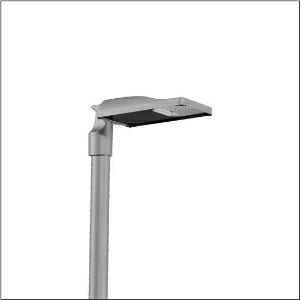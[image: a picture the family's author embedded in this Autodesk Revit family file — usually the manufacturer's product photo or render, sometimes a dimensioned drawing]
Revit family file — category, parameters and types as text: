
# Revit family: streetlight_sl_31_micro___st1_0a_5xh1d71b08ca_ebbd
name_source: partatom
category: Lighting Fixtures
units: mm (PartAtom-declared; Revit-internal decimal feet)

## family parameters
Cut with Voids When Loaded = No
Host = Face
Light Source = No
Part Type = Normal
Room Calculation Point = No
Round Connector Dimension = Use Diameter
Shared = No

## types (1)
- --- (1 x LED, 1170 lm, 10.3 W, 2200K)
    Apparent Load = 10 VA
    CIE Flux Codes = 37 72 97 100 100
    Color Rendering = 70
    Color Temperature = 2200K
    Default Elevation = 1800 mm
    Description = Streetlight SL 31 micro Easy, LST, Desk-Remote mast luminaire for post-top, side-entry; light control with lens of PMMA; light distribution: ST1.0a, direct asymmetric distribution, for standard-compliant lighting for roads and squares; LED: luminous flux: 1.170lm, light colour: 722, colour temperature: 2200K; luminous efficacy: 113,6lm/W; control: pre-setting: linear dimming characteristic, flexible luminous flux parameterisation, time-dependent luminous flux control, constant luminous flux control, power reduction, intelligent temperature release in ECG and LED module, overheat protection; luminaire housing, of diecast aluminium, SITECO metallic grey (DB 702S), corrosivity category C5 high according to DIN EN ISO 12944; cover of toughened safety glass, transparent, mast flange of diecast aluminium, SITECO metallic grey (DB 702S), spigot size: 76/60mm, mast flange included unmounted; cable length: 5,5m, connection cable pre-assembled; mains connection: 220..240V, AC, 50/60Hz; power consumption (at start of service life): 10,3W / (at end of service life): 10,6W / (with reduced operation 50%): 5,3W; protection rating (complete): IP66; insulation class (complete): insulation class II (safety insulation); impact resistance: IK10; certification: CE, ENEC, ENEC+, VDE, UKCA; permissible operating ambient temperature for outdoor applications: -40..+50°C; packaging unit: 1 piece

Light Distribution: ST1.0a
    Height = 76 mm
    Lamp = 1 x LED
    Lamp Light Flux = 1170 lm
    Lamp Power = 10.3 W
    Lamp count = 1
    Length = 467 mm
    Luminous efficacy = 114 lm/W
    Manufacturer = Siteco
    ModVariant = No
    Model = 5XH1D71B08CA
    Number of Poles = 1
    OnlyDefault = Yes
    Power Factor = 1
    Product Name = Streetlight SL 31 micro | ST1.0a
    Product group = mast luminaire | pylon top
    ProductGroupID = 6100
    Protection Class = Protection class II
    Protection Degree = IP 66
    RLX_Detail_Level = 1
    RLX_Emergency_Light_Flux = 0 lm
    RLX_Emergency_Type = 0
    RLX_Emergency_Type_DB = No
    RlxData = <blob elided: 22477 chars, md5=f99bd578>
    Socket = socket
    Standby Power = 0 W
    System Light Flux = 1170 lm
    System Power = 10 W
    Type Comments = factory setting: luminous flux: 100 % | dim-lin: 254 | 386 mA
    Type Image = l_1300309.jpg
    URL = http://relux.com
    VarID = @adj_009631
    Voltage = 0 V
    Weight = 0.00 kg
    Width = 265 mm

## geometry (parser evidence)
native form markers: Blend x4, Sweep x10
no freeform markers — native parametric forms only
